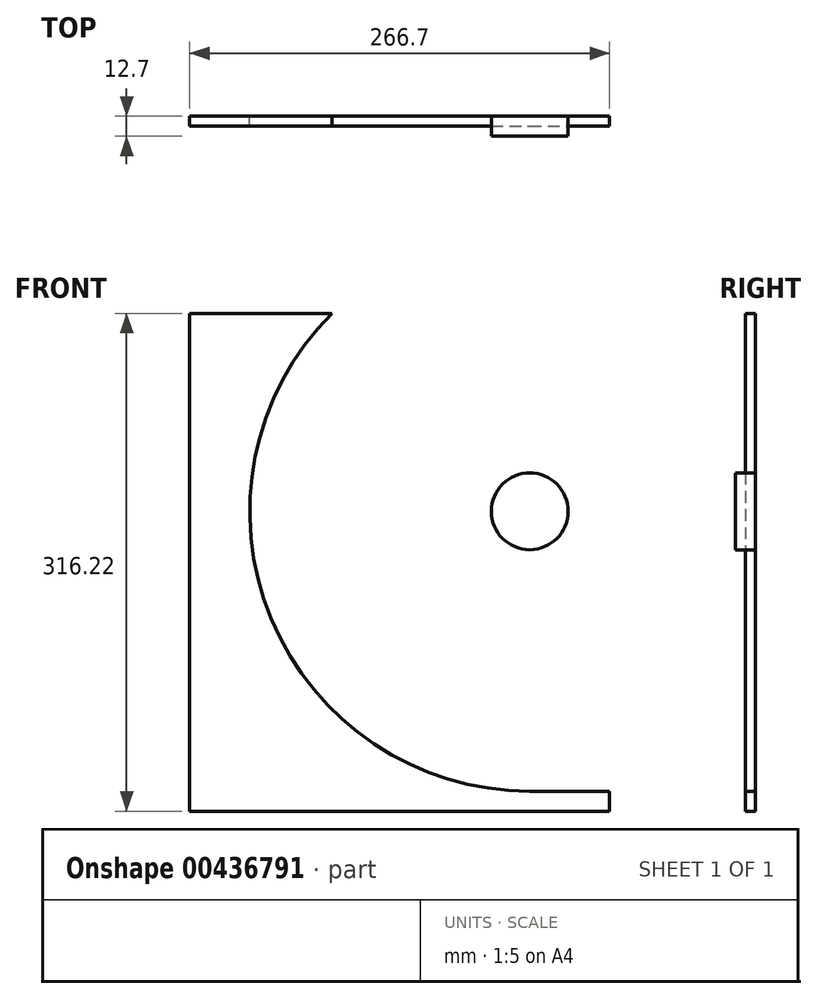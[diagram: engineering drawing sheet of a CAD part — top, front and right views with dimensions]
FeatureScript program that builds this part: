
annotation { "Feature Type Name" : "Feature", "Feature Type Description" : "" }
export const myFeature = defineFeature(function(context is Context, id is Id, definition is map)
    precondition{}
    {
        {
            var Q0;
            Q0=qCreatedBy(makeId("Front.planeOp"),FACE);
            var sketch = newSketch(context, id + "F0", { "sketchPlane" : qUnion([Q0])});
            skCircle(sketch, "E0", {"center": v(0, 0) * mm, "radius": 177.8 * mm});
            skLineSegment(sketch, "E1", {"start": v(0, 0) * mm, "end": v(-125.72, 125.72) * mm});
            skLineSegment(sketch, "E2", {"start": v(0, 0) * mm, "end": v(-177.8, 0) * mm});
            skLineSegment(sketch, "E3", {"start": v(-177.8, 0) * mm, "end": v(-215.9, 0) * mm});
            skLineSegment(sketch, "E4", {"start": v(-125.72, 125.72) * mm, "end": v(-215.9, 125.72) * mm});
            skLineSegment(sketch, "E5", {"start": v(0, -177.8) * mm, "end": v(50.8, -177.8) * mm});
            skLineSegment(sketch, "E6", {"start": v(50.8, -177.8) * mm, "end": v(50.8, -190.5) * mm});
            skLineSegment(sketch, "E7", {"start": v(50.8, -190.5) * mm, "end": v(-215.9, -190.5) * mm});
            skLineSegment(sketch, "E8", {"start": v(-215.9, -190.5) * mm, "end": v(-215.9, 125.72) * mm});
            skSolve(sketch);
        }
        {
            var Q0;
            {var subQ2=sQuery(id+"F0.wireOp",EDGE,"E3");Q0=makeQuery(id+"F0.imprint","IMPRINT",FACE,{"disambiguationData":[TD([[makeQuery(id+"F0.imprint","IMPRINT",EDGE,{"derivedFrom":subQ2}),-1.0]])]});}
            var Q1;
            {var subQ1=sQuery(id+"F0.wireOp",EDGE,"E3");Q1=makeQuery(id+"F0.imprint","IMPRINT",FACE,{"disambiguationData":[TD([[makeQuery(id+"F0.imprint","IMPRINT",EDGE,{"derivedFrom":subQ1}),1.0]])]});}
            extrude(context, id + "F1", {"entities" : qUnion([Q0, Q1]), "depth" : 6.35 * mm});
        }
        {
            var Q0;
            Q0=qCreatedBy(makeId("Front.planeOp"),FACE);
            var sketch = newSketch(context, id + "F2", { "sketchPlane" : qUnion([Q0])});
            skCircle(sketch, "E9", {"center": v(0, 0) * mm, "radius": 24.4 * mm});
            skSolve(sketch);
        }
        {
            var Q0;
            Q0=makeQuery(id+"F2.imprint","IMPRINT",FACE,{"disambiguationData":[TD([[makeQuery(id+"F2.imprint","IMPRINT",EDGE,{"derivedFrom":sQuery(id+"F2.wireOp",EDGE,"E9")}),1.0]])]});
            extrude(context, id + "F3", {"entities" : qUnion([Q0]), "depth" : 12.7 * mm});
        }
    });
